# Revit family: IS_Ceravito_B0406_BIM_DE
name_source: partatom
category: Plumbing Fixtures
revit_build: Autodesk Revit MEP 2016 (Build: 20161004_0715(x64)
units: mm (PartAtom-declared; Revit-internal decimal feet)

## family parameters
Always vertical = No
Cut with Voids When Loaded = No
OmniClass Number = 23.45.55.17
OmniClass Title = Mixing Faucets
Part Type = Normal
Room Calculation Point = No
Round Connector Dimension = Use Diameter
Shared = No
Work Plane-Based = No

## types (1)
- B0406AA CERAVITO single lever one hole basin mixer with pop-up waste
    Accessories = www.idealstandard.de\ersatzteile
    AssetType = Fixed
    BIMObjectName = ISI_IdealStandard_WashbasinTaps_Ceravito_B0406AA
    BIMobject category = Taps & Mixers
    BOSUseNativeGeometries = 1
    BarCode = 3800861039464
    Brand = Ideal Standard
    Brand url = http://www.idealstandard.de
    CodePerformance = EN 817, DIN 4109, Gruppe 1
    Color = Chrome
    ConnectionType = Plumbing
    Cost = 0 $
    CurrencyUnit = €
    CurrentRevision = 1
    Date of publishing = 20/12/2017
    Description = IS Waschtischarmatur CERAVITO, 5l/min., m.Ablgarn., Ausld.101mm, Chrom
    DurationUnit = Year
    EAN code = https://3800861039464
    Edition number = 1
    ExpectedLife = 25
    Features = IS Waschtischarmatur CERAVITO, 5l/min., m.Ablgarn., Ausld.101mm, Chrom
    Finish = Chrome
    IFC Classification = Sanitary Terminal
    IfcExportAs = IfcSanitaryTerminalType
    InletConnectionSize = 0 mm  [stored 0 ft]
    Installation instructions = http://www.idealstandard.de
    InstallationInstructions = www.idealstandard.de\produkte
    MainColor = Chrome
    MaintenanceInformation = www.idealstandard.de\produkte
    Manufacturer name = Ideal Standard
    ManufacturerURL = http://www.idealstandard.de
    Material = Brass
    Material main = Brass
    Model = B0406AA
    ModelNumber = B0406AA
    ModelReference = IS Waschtischarmatur CERAVITO, 5l/min., m.Ablgarn., Ausld.101mm, Chrom
    NBS Reference Code = 35-79-95
    NBS Reference Description = Wash Basin And Trough Water Supply Fittings
    Name = WashbasinTaps_Ceravito_B0406AA
    NettWeight = 1.51 Kg
    Nominal height = 0
    Nominal width = 0
    NominalDepth = 137 mm
    NominalHeight = 137 mm
    NominalLength = 137 mm
    NominalWidth = 51 mm
    OmniClass Code = 23-31 11 00
    OmniClass Description = Faucets
    Product Guid = 4213d1a1-836b-4e68-8395-d50859ee170e
    Product SKU = B0406
    Product data url = https://bimobject.com
    Product family = Sanitary
    Product group = Basin Mixer
    Product name = CERAVITO single lever one hole basin mixer with pop-up waste
    Product url = http://www.idealstandard.de
    ProductInformation = www.idealstandard.de/produkte
    QR code = http://bimobject.com
    Shape = Sculptured
    Size = 52x137x137 mm
    Space = Internal
    SpareParts = www.idealstandard.de/ersatzteile
    Technical description = http://www.idealstandard.de
    TestPressure = 10 Bar
    URL = http://www.idealstandard.de
    Uniclass 1.4 Code = L8212
    Uniclass 1.4 Description = Fittings
    Uniclass 2.0 Code = PR-35-79-95
    Uniclass 2.0 Description = Wash Basin And Trough Water Supply Fittings
    Uniclass 2015 Code = Pr_40_20_87_96
    Uniclass 2015 Name = Washbasin manual water supply sets
    Uniclass2015Code = Pr_40_20_87_98
    Uniclass2015Title = Washbasin taps
    Uniclass2015Version = Products v1.1
    Version = 1
    VolumeUnits = Litres
    Weight Net (Kg) = 1.51

note: [stored X ft] marks values corroborated as IEEE doubles in the binary element streams (Revit-internal decimal feet)

## geometry (parser evidence)
native form markers: Blend x2, Sweep x3
no freeform markers — native parametric forms only
